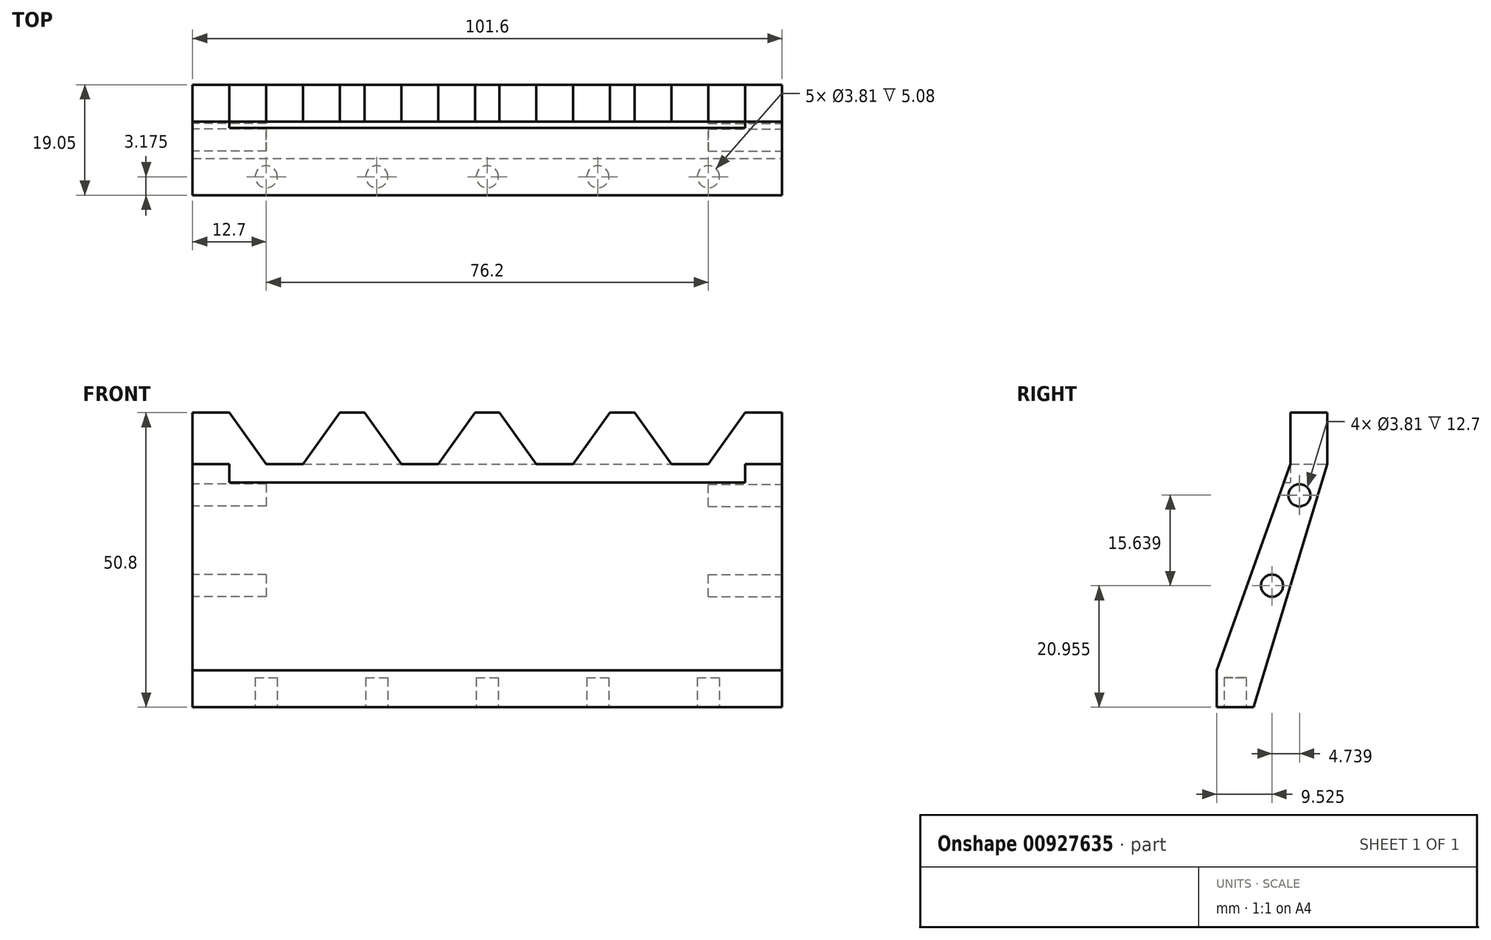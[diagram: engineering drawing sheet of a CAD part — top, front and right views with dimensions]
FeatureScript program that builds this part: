
annotation { "Feature Type Name" : "Feature", "Feature Type Description" : "" }
export const myFeature = defineFeature(function(context is Context, id is Id, definition is map)
    precondition{}
    {
        {
            var Q0;
            Q0=qCreatedBy(makeId("Front.planeOp"),FACE);
            var sketch = newSketch(context, id + "F0", { "sketchPlane" : qUnion([Q0])});
            skLineSegment(sketch, "E0.bottom", {"start": v(50.8, 25.4) * mm, "end": v(44.44, 25.4) * mm});
            skLineSegment(sketch, "E0.top", {"start": v(50.8, -25.4) * mm, "end": v(-50.8, -25.4) * mm});
            skLineSegment(sketch, "E0.left", {"start": v(50.8, 25.4) * mm, "end": v(50.8, -25.4) * mm});
            skLineSegment(sketch, "E0.right", {"start": v(-50.8, 25.4) * mm, "end": v(-50.8, -25.4) * mm});
            skPoint(sketch, "E0.middle", {"position": v(0, 0) * mm});
            skLineSegment(sketch, "E1.bottom", {"start": v(-50.8, 16.5) * mm, "end": v(-44.45, 16.5) * mm});
            skLineSegment(sketch, "E1.top", {"start": v(-50.8, -25.4) * mm, "end": v(-44.45, -25.4) * mm});
            skLineSegment(sketch, "E1.left", {"start": v(-50.8, 16.5) * mm, "end": v(-50.8, -25.4) * mm});
            skLineSegment(sketch, "E1.right", {"start": v(-44.45, 16.5) * mm, "end": v(-44.45, -19.05) * mm});
            skLineSegment(sketch, "E2.MirrorCS", {"start": v(44.45, 16.5) * mm, "end": v(44.45, -19.05) * mm});
            skLineSegment(sketch, "E3.MirrorCS", {"start": v(50.8, 16.5) * mm, "end": v(44.45, 16.5) * mm});
            skLineSegment(sketch, "E4.bottom", {"start": v(44.45, -25.4) * mm, "end": v(-44.45, -25.4) * mm});
            skLineSegment(sketch, "E4.top", {"start": v(44.45, -19.05) * mm, "end": v(-44.45, -19.05) * mm});
            skLineSegment(sketch, "E5", {"start": v(-44.45, 25.4) * mm, "end": v(-38.1, 16.5) * mm});
            skLineSegment(sketch, "E6", {"start": v(-38.1, 16.5) * mm, "end": v(-31.75, 16.5) * mm});
            skLineSegment(sketch, "E7", {"start": v(-31.75, 16.5) * mm, "end": v(-25.4, 25.4) * mm});
            skLineSegment(sketch, "E8", {"start": v(-25.4, 25.4) * mm, "end": v(-20.72, 25.4) * mm});
            skLineSegment(sketch, "E9", {"start": v(-2.12, 25.4) * mm, "end": v(2.1, 25.4) * mm});
            skLineSegment(sketch, "E10", {"start": v(21.16, 25.4) * mm, "end": v(25.39, 25.4) * mm});
            skLineSegment(sketch, "E11.trimOffspring", {"start": v(-44.45, 25.4) * mm, "end": v(-50.8, 25.4) * mm});
            skLineSegment(sketch, "E12.1.0.0", {"start": v(-8.47, 16.5) * mm, "end": v(-2.12, 25.4) * mm});
            skLineSegment(sketch, "E12.1.0.1", {"start": v(-14.82, 16.5) * mm, "end": v(-8.47, 16.5) * mm});
            skLineSegment(sketch, "E12.1.0.2", {"start": v(-21.17, 25.4) * mm, "end": v(-14.82, 16.51) * mm});
            skLineSegment(sketch, "E12.2.0.0", {"start": v(14.8, 16.5) * mm, "end": v(21.16, 25.4) * mm});
            skLineSegment(sketch, "E12.2.0.1", {"start": v(8.46, 16.5) * mm, "end": v(14.8, 16.5) * mm});
            skLineSegment(sketch, "E12.2.0.2", {"start": v(2.1, 25.4) * mm, "end": v(8.46, 16.51) * mm});
            skLineSegment(sketch, "E12.3.0.0", {"start": v(38.09, 16.5) * mm, "end": v(44.44, 25.4) * mm});
            skLineSegment(sketch, "E12.3.0.1", {"start": v(31.74, 16.5) * mm, "end": v(38.09, 16.5) * mm});
            skLineSegment(sketch, "E12.3.0.2", {"start": v(25.39, 25.4) * mm, "end": v(31.74, 16.51) * mm});
            skLineSegment(sketch, "E12.direction1", {"start": v(-38.1, 16.5) * mm, "end": v(-14.82, 16.5) * mm, "construction": true});
            skLineSegment(sketch, "E13.trimOffspring", {"start": v(-20.72, 25.4) * mm, "end": v(-25.4, 25.4) * mm});
            skLineSegment(sketch, "E14.trimOffspring", {"start": v(2.1, 25.4) * mm, "end": v(-2.12, 25.4) * mm});
            skLineSegment(sketch, "E15.trimOffspring", {"start": v(25.39, 25.4) * mm, "end": v(21.16, 25.4) * mm});
            skLineSegment(sketch, "E16", {"start": v(-44.45, 13.33) * mm, "end": v(44.45, 13.34) * mm});
            skSolve(sketch);
        }
        {
            var Q0;
            {var subQ4=sQuery(id+"F0.wireOp",EDGE,"E0.bottom");Q0=makeQuery(id+"F0.imprint","IMPRINT",FACE,{"disambiguationData":[TD([[makeQuery(id+"F0.imprint","IMPRINT",EDGE,{"derivedFrom":subQ4}),1.0]])]});}
            extrude(context, id + "F1", {"entities" : qUnion([Q0]), "depth" : 6.35 * mm, "offsetDistance" : 25.4 * mm});
        }
        {
            var Q0;
            {var subQ8=sQuery(id+"F0.wireOp",EDGE,"E0.top");Q0=makeQuery(id+"F0.imprint","IMPRINT",FACE,{"disambiguationData":[TD([[makeQuery(id+"F0.imprint","IMPRINT",EDGE,{"derivedFrom":subQ8}),-1.0]])]});}
            var Q1;
            {var subQ0=sQuery(id+"F0.wireOp",EDGE,"E4.top");Q1=makeQuery(id+"F0.imprint","IMPRINT",FACE,{"disambiguationData":[TD([[makeQuery(id+"F0.imprint","IMPRINT",EDGE,{"derivedFrom":subQ0}),-1.0]])]});}
            extrude(context, id + "F2", {"entities" : qUnion([Q0, Q1]), "operationType" : NewBodyOperationType.ADD, "depth" : 19.05 * mm, "offsetDistance" : 25.4 * mm});
        }
        {
            var Q0;
            {var subQ0=sQuery(id+"F0.wireOp",EDGE,"E0.left");Q0=makeQuery(id+"F2.boolean.opBoolean","MERGE",FACE,{"derivedFrom":[makeQuery(id+"F1.opExtrude","SWEPT_FACE",FACE,{"disambiguationData":[OSD([subQ0])]}),makeQuery(id+"F2.opExtrude","SWEPT_FACE",FACE,{"disambiguationData":[OSD([subQ0])]})]});}
            var Q1;
            Q1 = qBodyType(qCreatedBy(id + "F4" ,EDGE), BodyType.WIRE);
            cPlane(context, id + "F3", {"entities" : qUnion([Q0, Q1]), "cplaneType" : CPlaneType.OFFSET, "offset" : 0 * mm, "width" : 152.4 * mm, "height" : 152.4 * mm});
        }
        {
            var Q0;
            Q0=qCreatedBy(id+"F3.planeOp",FACE);
            var sketch = newSketch(context, id + "F4", { "sketchPlane" : qUnion([Q0])});
            skLineSegment(sketch, "E17.bottom", {"start": v(0, -25.4) * mm, "end": v(-19.05, -25.4) * mm});
            skLineSegment(sketch, "E17.top", {"start": v(0, 25.4) * mm, "end": v(-19.05, 25.4) * mm});
            skLineSegment(sketch, "E17.left", {"start": v(0, -25.4) * mm, "end": v(0, 25.4) * mm});
            skLineSegment(sketch, "E17.right", {"start": v(-19.05, -25.4) * mm, "end": v(-19.05, 25.4) * mm});
            skLineSegment(sketch, "E18.bottom", {"start": v(-6.35, 25.4) * mm, "end": v(0, 25.4) * mm});
            skLineSegment(sketch, "E18.top", {"start": v(-6.35, 16.5) * mm, "end": v(0, 16.5) * mm});
            skLineSegment(sketch, "E18.left", {"start": v(-6.35, 25.4) * mm, "end": v(-6.35, 16.5) * mm});
            skLineSegment(sketch, "E18.right", {"start": v(0, 25.4) * mm, "end": v(0, 16.5) * mm});
            skLineSegment(sketch, "E19", {"start": v(-6.35, 16.51) * mm, "end": v(-19.05, -19.05) * mm});
            skLineSegment(sketch, "E20", {"start": v(0, 16.5) * mm, "end": v(-12.7, -25.4) * mm});
            skLineSegment(sketch, "E21", {"start": v(-15.87, -25.4) * mm, "end": v(-10.08, -6.27) * mm});
            skCircle(sketch, "E22", {"center": v(-9.52, -4.45) * mm, "radius": 1.9 * mm});
            skCircle(sketch, "E23", {"center": v(-4.8, 11.14) * mm, "radius": 1.9 * mm});
            skLineSegment(sketch, "E24.trimOffspring", {"start": v(-8.97, -2.62) * mm, "end": v(-5.36, 9.32) * mm});
            skLineSegment(sketch, "E25.trimOffspring", {"start": v(-4.25, 12.96) * mm, "end": v(-3.17, 16.51) * mm});
            skSolve(sketch);
        }
        {
            var Q0;
            {var subQ0=sQuery(id+"F4.wireOp",EDGE,"E17.left");Q0=makeQuery(id+"F4.imprint","IMPRINT",FACE,{"disambiguationData":[TD([[makeQuery(id+"F4.imprint","IMPRINT",EDGE,{"derivedFrom":subQ0}),1.0]])]});}
            var Q1;
            {var subQ0=sQuery(id+"F4.wireOp",EDGE,"E17.top");Q1=makeQuery(id+"F4.imprint","IMPRINT",FACE,{"disambiguationData":[TD([[makeQuery(id+"F4.imprint","IMPRINT",EDGE,{"derivedFrom":subQ0}),1.0]])]});}
            extrude(context, id + "F5", {"entities" : qUnion([Q0, Q1]), "operationType" : NewBodyOperationType.REMOVE, "oppositeDirection" : true, "depth" : 101.6 * mm, "offsetDistance" : 25.4 * mm});
        }
        {
            var Q0;
            {var subQ0=sQuery(id+"F4.wireOp",EDGE,"E22");var subQ1=makeQuery(id+"F4.imprint","INTERSECT",VERTEX,{"derivedFrom":[sQuery(id+"F4.wireOp",EDGE,"E21"),subQ0]});Q0=makeQuery(id+"F4.imprint","IMPRINT",FACE,{"disambiguationData":[TD([[makeQuery(id+"F4.imprint","IMPRINT",EDGE,{"disambiguationData":[TD([[subQ1,1.0]])],"derivedFrom":subQ0}),1.0]])]});}
            var Q1;
            {var subQ0=sQuery(id+"F4.wireOp",EDGE,"E23");var subQ1=makeQuery(id+"F4.imprint","INTERSECT",VERTEX,{"derivedFrom":[subQ0,sQuery(id+"F4.wireOp",EDGE,"E24.trimOffspring")]});Q1=makeQuery(id+"F4.imprint","IMPRINT",FACE,{"disambiguationData":[TD([[makeQuery(id+"F4.imprint","IMPRINT",EDGE,{"disambiguationData":[TD([[subQ1,1.0]])],"derivedFrom":subQ0}),1.0]])]});}
            var Q2;
            Q2 = qSketchRegion(id + "F8", true);
            extrude(context, id + "F6", {"entities" : qUnion([Q0, Q1, Q2]), "operationType" : NewBodyOperationType.REMOVE, "oppositeDirection" : true, "depth" : 12.7 * mm, "offsetDistance" : 25.4 * mm});
        }
        {
            var Q0;
            Q0=makeQuery(id+"F2.boolean.opBoolean","MERGE",FACE,{"derivedFrom":[makeQuery(id+"F1.opExtrude","SWEPT_FACE",FACE,{"disambiguationData":[OSD([sQuery(id+"F0.wireOp",EDGE,"E0.right")])]}),makeQuery(id+"F2.opExtrude","SWEPT_FACE",FACE,{"disambiguationData":[OSD([sQuery(id+"F0.wireOp",EDGE,"E1.left")])]})]});
            cPlane(context, id + "F7", {"entities" : qUnion([Q0]), "cplaneType" : CPlaneType.OFFSET, "offset" : 0 * mm, "width" : 152.4 * mm, "height" : 152.4 * mm});
        }
        {
            var Q0;
            Q0=qCreatedBy(id+"F7.planeOp",FACE);
            var sketch = newSketch(context, id + "F8", { "sketchPlane" : qUnion([Q0])});
            skLineSegment(sketch, "E26.bottom", {"start": v(0, -25.4) * mm, "end": v(19.05, -25.4) * mm});
            skLineSegment(sketch, "E26.top", {"start": v(0, 25.4) * mm, "end": v(19.05, 25.4) * mm});
            skLineSegment(sketch, "E26.left", {"start": v(0, -25.4) * mm, "end": v(0, 25.4) * mm});
            skLineSegment(sketch, "E26.right", {"start": v(19.05, -25.4) * mm, "end": v(19.05, 25.4) * mm});
            skLineSegment(sketch, "E27", {"start": v(12.7, -25.4) * mm, "end": v(0, 16.51) * mm});
            skLineSegment(sketch, "E28", {"start": v(19.05, -19.05) * mm, "end": v(6.35, 16.5) * mm});
            skLineSegment(sketch, "E29", {"start": v(6.35, 16.5) * mm, "end": v(6.35, 25.4) * mm});
            skLineSegment(sketch, "E30", {"start": v(3.17, 16.51) * mm, "end": v(4.23, 13.02) * mm});
            skCircle(sketch, "E31", {"center": v(9.53, -4.45) * mm, "radius": 1.9 * mm});
            skCircle(sketch, "E32", {"center": v(4.79, 11.2) * mm, "radius": 1.9 * mm});
            skLineSegment(sketch, "E33.trimOffspring", {"start": v(5.34, 9.37) * mm, "end": v(8.97, -2.62) * mm});
            skLineSegment(sketch, "E34.trimOffspring", {"start": v(10.08, -6.27) * mm, "end": v(15.88, -25.4) * mm});
            skSolve(sketch);
        }
        {
            var Q0;
            {var subQ0=sQuery(id+"F8.wireOp",EDGE,"E32");var subQ1=makeQuery(id+"F8.imprint","IMPRINT",VERTEX,{"disambiguationData":[OD(0.0)],"derivedFrom":subQ0});Q0=makeQuery(id+"F8.imprint","IMPRINT",FACE,{"disambiguationData":[TD([[makeQuery(id+"F8.imprint","IMPRINT",EDGE,{"disambiguationData":[TD([[subQ1,-1.0]])],"derivedFrom":subQ0}),1.0]])]});}
            var Q1;
            {var subQ0=sQuery(id+"F8.wireOp",EDGE,"E31");var subQ1=makeQuery(id+"F8.imprint","IMPRINT",VERTEX,{"disambiguationData":[OD(0.0)],"derivedFrom":subQ0});Q1=makeQuery(id+"F8.imprint","IMPRINT",FACE,{"disambiguationData":[TD([[makeQuery(id+"F8.imprint","IMPRINT",EDGE,{"disambiguationData":[TD([[subQ1,-1.0]])],"derivedFrom":subQ0}),1.0]])]});}
            extrude(context, id + "F9", {"entities" : qUnion([Q0, Q1]), "operationType" : NewBodyOperationType.REMOVE, "oppositeDirection" : true, "depth" : 12.7 * mm, "offsetDistance" : 25.4 * mm});
        }
        {
            var Q0;
            Q0=makeQuery(id+"F2.opExtrude","SWEPT_FACE",FACE,{"disambiguationData":[OSD([sQuery(id+"F0.wireOp",EDGE,"E0.top"),sQuery(id+"F0.wireOp",EDGE,"E1.top"),sQuery(id+"F0.wireOp",EDGE,"E4.bottom")])]});
            cPlane(context, id + "F10", {"entities" : qUnion([Q0]), "cplaneType" : CPlaneType.OFFSET, "offset" : 0 * mm, "width" : 152.4 * mm, "height" : 152.4 * mm});
        }
        {
            var Q0;
            Q0=qCreatedBy(id+"F10.planeOp",FACE);
            var sketch = newSketch(context, id + "F11", { "sketchPlane" : qUnion([Q0])});
            skLineSegment(sketch, "E35.bottom", {"start": v(-50.8, 19.05) * mm, "end": v(50.8, 19.05) * mm});
            skLineSegment(sketch, "E35.top", {"start": v(-50.8, 12.7) * mm, "end": v(50.8, 12.7) * mm});
            skLineSegment(sketch, "E35.left", {"start": v(-50.8, 19.05) * mm, "end": v(-50.8, 12.7) * mm});
            skLineSegment(sketch, "E35.right", {"start": v(50.8, 19.05) * mm, "end": v(50.8, 12.7) * mm});
            skCircle(sketch, "E36", {"center": v(-38.1, 15.87) * mm, "radius": 1.9 * mm});
            skCircle(sketch, "E37", {"center": v(-19.05, 15.87) * mm, "radius": 1.9 * mm});
            skCircle(sketch, "E38", {"center": v(0, 15.87) * mm, "radius": 1.9 * mm});
            skCircle(sketch, "E39", {"center": v(19.05, 15.87) * mm, "radius": 1.9 * mm});
            skCircle(sketch, "E40", {"center": v(38.1, 15.87) * mm, "radius": 1.9 * mm});
            skSolve(sketch);
        }
        {
            var Q0;
            Q0=makeQuery(id+"F11.imprint","IMPRINT",FACE,{"disambiguationData":[TD([[makeQuery(id+"F11.imprint","IMPRINT",EDGE,{"derivedFrom":sQuery(id+"F11.wireOp",EDGE,"E36")}),1.0]])]});
            var Q1;
            Q1=makeQuery(id+"F11.imprint","IMPRINT",FACE,{"disambiguationData":[TD([[makeQuery(id+"F11.imprint","IMPRINT",EDGE,{"derivedFrom":sQuery(id+"F11.wireOp",EDGE,"E37")}),1.0]])]});
            var Q2;
            Q2=makeQuery(id+"F11.imprint","IMPRINT",FACE,{"disambiguationData":[TD([[makeQuery(id+"F11.imprint","IMPRINT",EDGE,{"derivedFrom":sQuery(id+"F11.wireOp",EDGE,"E38")}),1.0]])]});
            var Q3;
            Q3=makeQuery(id+"F11.imprint","IMPRINT",FACE,{"disambiguationData":[TD([[makeQuery(id+"F11.imprint","IMPRINT",EDGE,{"derivedFrom":sQuery(id+"F11.wireOp",EDGE,"E39")}),1.0]])]});
            var Q4;
            Q4=makeQuery(id+"F11.imprint","IMPRINT",FACE,{"disambiguationData":[TD([[makeQuery(id+"F11.imprint","IMPRINT",EDGE,{"derivedFrom":sQuery(id+"F11.wireOp",EDGE,"E40")}),1.0]])]});
            extrude(context, id + "F12", {"entities" : qUnion([Q0, Q1, Q2, Q3, Q4]), "operationType" : NewBodyOperationType.REMOVE, "oppositeDirection" : true, "depth" : 5.08 * mm, "offsetDistance" : 25.4 * mm});
        }
    });
